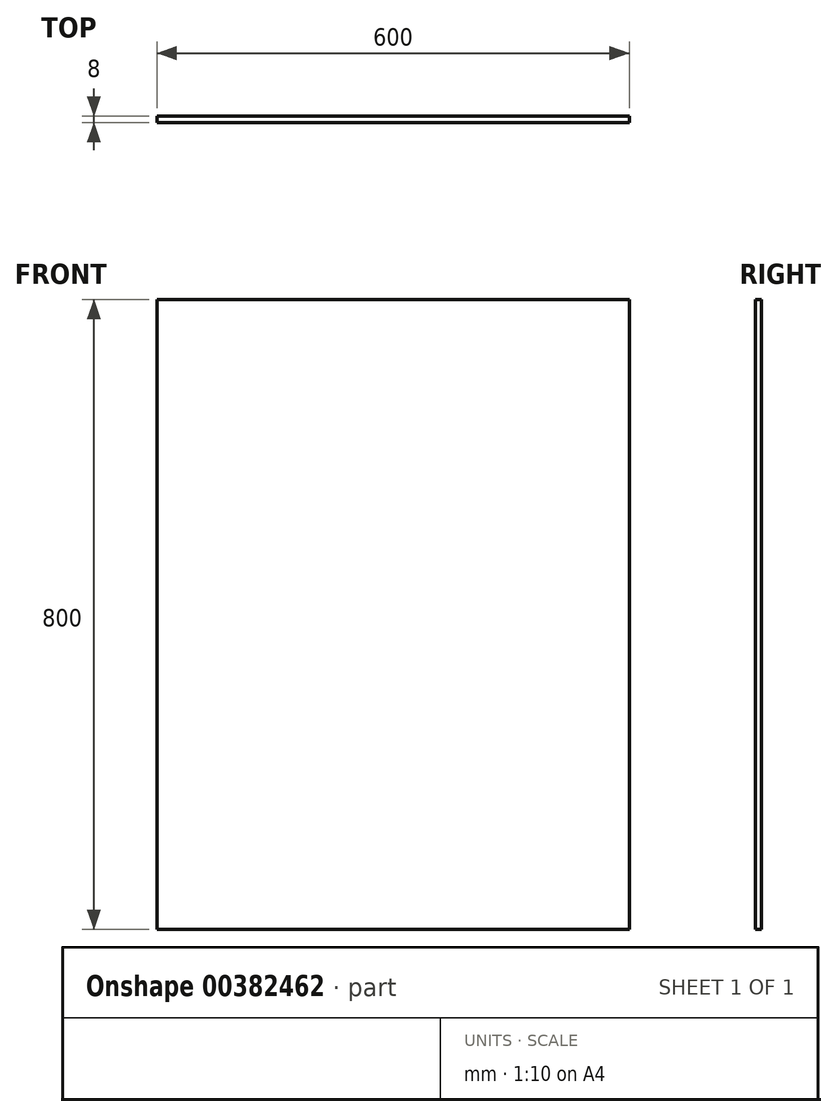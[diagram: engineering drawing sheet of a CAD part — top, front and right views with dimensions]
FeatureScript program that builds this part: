
annotation { "Feature Type Name" : "Feature", "Feature Type Description" : "" }
export const myFeature = defineFeature(function(context is Context, id is Id, definition is map)
    precondition{}
    {
        {
            var Q0;
            Q0=qCreatedBy(makeId("Front.planeOp"),FACE);
            var sketch = newSketch(context, id + "F0", { "sketchPlane" : qUnion([Q0])});
            skLineSegment(sketch, "E0.bottom", {"start": v(-300, 400) * mm, "end": v(300, 400) * mm});
            skLineSegment(sketch, "E0.top", {"start": v(-300, -400) * mm, "end": v(300, -400) * mm});
            skLineSegment(sketch, "E0.left", {"start": v(-300, 400) * mm, "end": v(-300, -400) * mm});
            skLineSegment(sketch, "E0.right", {"start": v(300, 400) * mm, "end": v(300, -400) * mm});
            skPoint(sketch, "E0.middle", {"position": v(0, 0) * mm});
            skSolve(sketch);
        }
        {
            var Q0;
            Q0=makeQuery(id+"F0.imprint","IMPRINT",FACE,{"disambiguationData":[TD([[makeQuery(id+"F0.imprint","IMPRINT",EDGE,{"derivedFrom":sQuery(id+"F0.wireOp",EDGE,"E0.bottom")}),-1.0]])]});
            extrude(context, id + "F1", {"entities" : qUnion([Q0]), "endBound" : BoundingType.SYMMETRIC, "depth" : 8 * mm});
        }
    });
